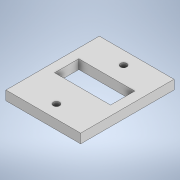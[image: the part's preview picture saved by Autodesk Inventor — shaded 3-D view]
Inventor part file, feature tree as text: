
AUTODESK INVENTOR PART (.ipt)
format: ipt  version: 2020.3 (Build 243373000, 373)  size: 243,712 bytes
history: native  units: mm
features: extrude x1, sketch x1
ambient origin geometry x8: Origin, YZ Plane, XZ Plane, XY Plane, X Axis, Y Axis, Z Axis, Center Point
bodies: Solid1 (feature_tree)
feature tree (2):
  extrude  "Extrusion1"  Depth=50.0mm
  sketch  "Sketch1"  dims[d0=40.0mm d1=50.0mm d2=3.4mm d3=3.4mm d4=5.0mm d5=0.0mm d6=19.0mm]
